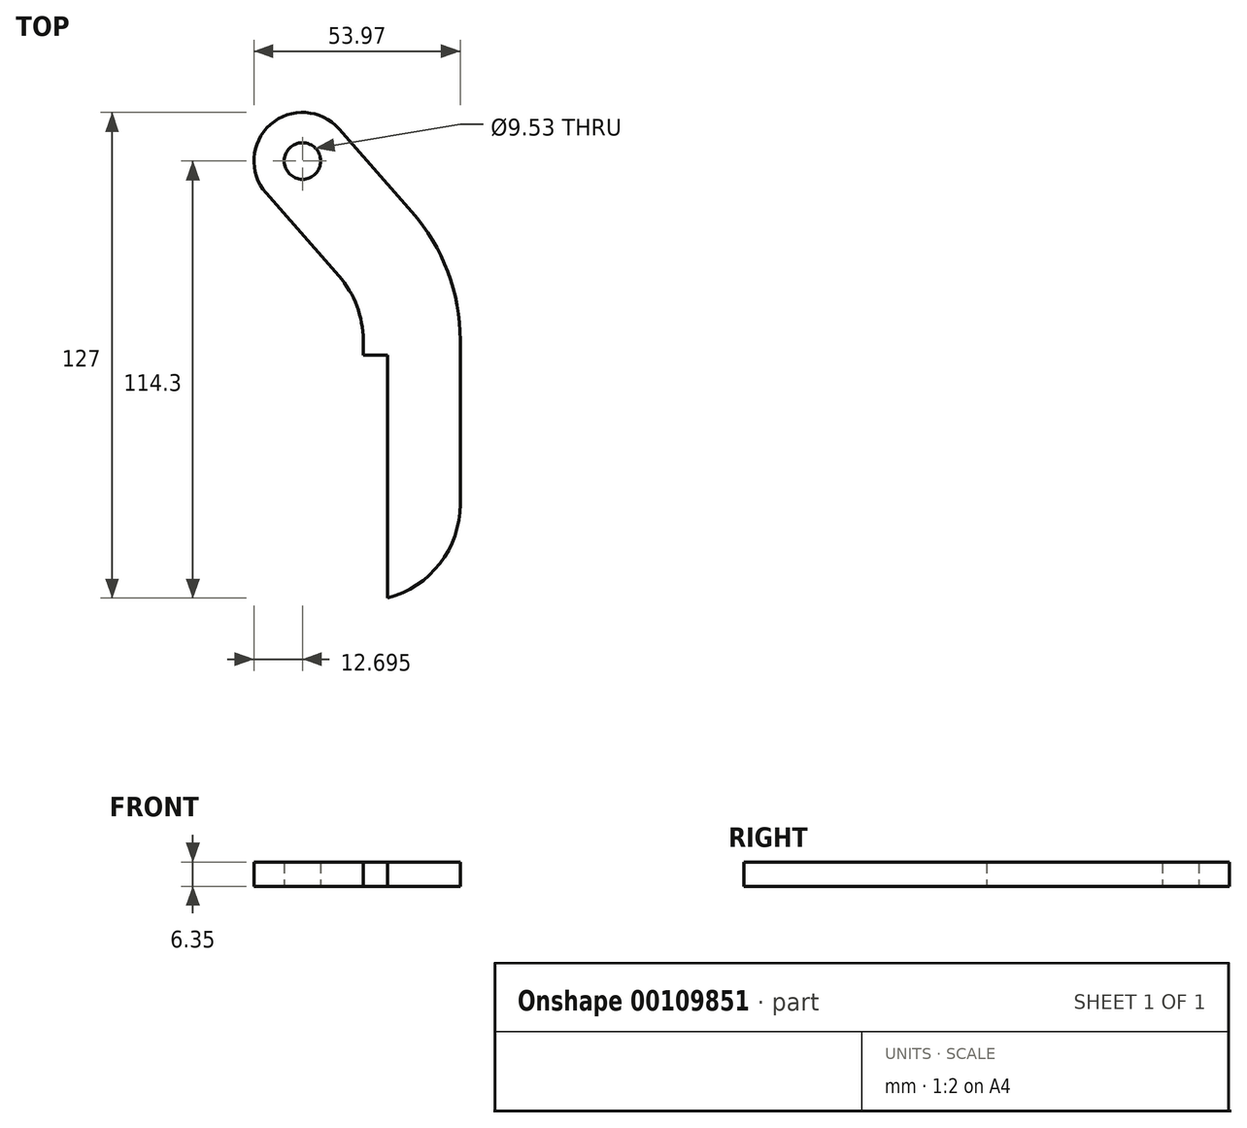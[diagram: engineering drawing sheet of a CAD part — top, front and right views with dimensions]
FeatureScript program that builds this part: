
annotation { "Feature Type Name" : "Feature", "Feature Type Description" : "" }
export const myFeature = defineFeature(function(context is Context, id is Id, definition is map)
    precondition{}
    {
        {
            var Q0;
            Q0=qCreatedBy(makeId("Top.planeOp"),FACE);
            var sketch = newSketch(context, id + "F0", { "sketchPlane" : qUnion([Q0])});
            skCircle(sketch, "E0", {"center": v(-15.88, 50.8) * mm, "radius": 4.76 * mm});
            skLineSegment(sketch, "E1", {"start": v(25.4, 23.07) * mm, "end": v(25.4, -63.5) * mm});
            skLineSegment(sketch, "E2", {"start": v(25.4, -63.5) * mm, "end": v(6.35, -63.5) * mm});
            skLineSegment(sketch, "E3", {"start": v(6.35, -63.5) * mm, "end": v(6.35, 0) * mm});
            skLineSegment(sketch, "E4", {"start": v(6.35, 0) * mm, "end": v(0, 0) * mm});
            skPoint(sketch, "E5.end.orphan", {"position": v(0, 38.9) * mm});
            skLineSegment(sketch, "E6", {"start": v(0, 13.5) * mm, "end": v(-25.42, 42.42) * mm});
            skLineSegment(sketch, "E7.0", {"start": v(25.4, 23.07) * mm, "end": v(-6.33, 59.18) * mm});
            skArc(sketch, "E8", {"start": v(-6.33, 59.18) * mm, "mid": v(-24.26, 60.34) * mm, "end": v(-25.42, 42.42) * mm});
            skLineSegment(sketch, "E9", {"start": v(0, 13.5) * mm, "end": v(0, 0) * mm});
            skSolve(sketch);
        }
        {
            var Q0;
            Q0=qSketchRegion(id+"F0",true);
            extrude(context, id + "F1", {"entities" : qUnion([Q0]), "depth" : 6.35 * mm});
        }
        {
            var Q0;
            Q0=makeQuery(id+"F1.opExtrude","SWEPT_EDGE",EDGE,{"disambiguationData":[OSD([sQuery(id+"F0.wireOp",EDGE,"E6"),sQuery(id+"F0.wireOp",EDGE,"E9")])]});
            var Q1;
            Q1=makeQuery(id+"F1.opExtrude","SWEPT_EDGE",EDGE,{"disambiguationData":[OSD([sQuery(id+"F0.wireOp",EDGE,"E1"),sQuery(id+"F0.wireOp",EDGE,"E2")])]});
            fillet(context, id + "F2", {"entities" : qUnion([Q0, Q1]), "radius" : 25.4 * mm, "tangentPropagation" : true, "allowEdgeOverflow" : false});
        }
        {
            var Q0;
            Q0=makeQuery(id+"F1.opExtrude","SWEPT_EDGE",EDGE,{"disambiguationData":[OSD([sQuery(id+"F0.wireOp",EDGE,"E1"),sQuery(id+"F0.wireOp",EDGE,"E7.0")])]});
            fillet(context, id + "F3", {"entities" : qUnion([Q0]), "radius" : 50.8 * mm, "tangentPropagation" : true, "allowEdgeOverflow" : false});
        }
    });
